# Revit family: HL_Трап для балконов и террас_HL5100THG
name_source: partatom
category: Instalační zařizovací předměty
revit_build: Autodesk Revit 2016 (Build: 20151007_0715(x64)
units: mm (PartAtom-declared; Revit-internal decimal feet)

## family parameters
Bod výpočtu místnosti = Ano
Kóta kulaté spojky = Použít průměr
Nadpis OmniClass = Deck Waste Water Drains
Ořezat dutým tvarem při načtení = Ne
Sdílené = Ne
Typ součásti = Normální
Vždy vertikální = Ano
Založené na pracovní rovině = Ne
Číslo OmniClass = 23.70.50.21.24.14

## types (1)
- HL_Трап для балконов и террас_HL5100THG
    EAN = 9003076048816
    Klíčová poznámka = HL5100THG
    Komentáře k typům = Трап с горизонтальным выпуском DN75, битумным полотном, незамерзающим запахозапирающим устройством, чугунные подрамник 190х190 мм и решётка 175х175 мм
    Model = HL5100THG
    Popis = Трап для балконов и террас
    Připojení CW = Ne
    Připojení HW = Ne
    Připojení odpadu = Ano
    Připojení ventilace = Ne
    URL = https://www.hutterer-lechner.com
    Výrobce = HL Hutterer & Lechner GmbH
    ВЕС = 13,715 kg
    ВЫСОТА МОНТАЖА = 147mm (102mm+45mm)
    МАКСИМАЛЬНАЯ НАГРУЗКА КЛАССА = B - max. 12,5t
    МАТЕРИАЛ = PP/GG/Bitumen
    НАСАДКА = 45-75mm/190x190mm Guss
    НОМИНАЛЬНЫЙ ДИАМЕТР = 75 mm
    ПРОИЗВОДИТЕЛЬНОСТЬ = 2,9l/s
    РАЗМЕР = DN75
    РЕШЁТКА = 175x175mm Guss
    Угол установки = 90.00°

## geometry (parser evidence)
native form markers: Blend x4, Sweep x21
no freeform markers — native parametric forms only
